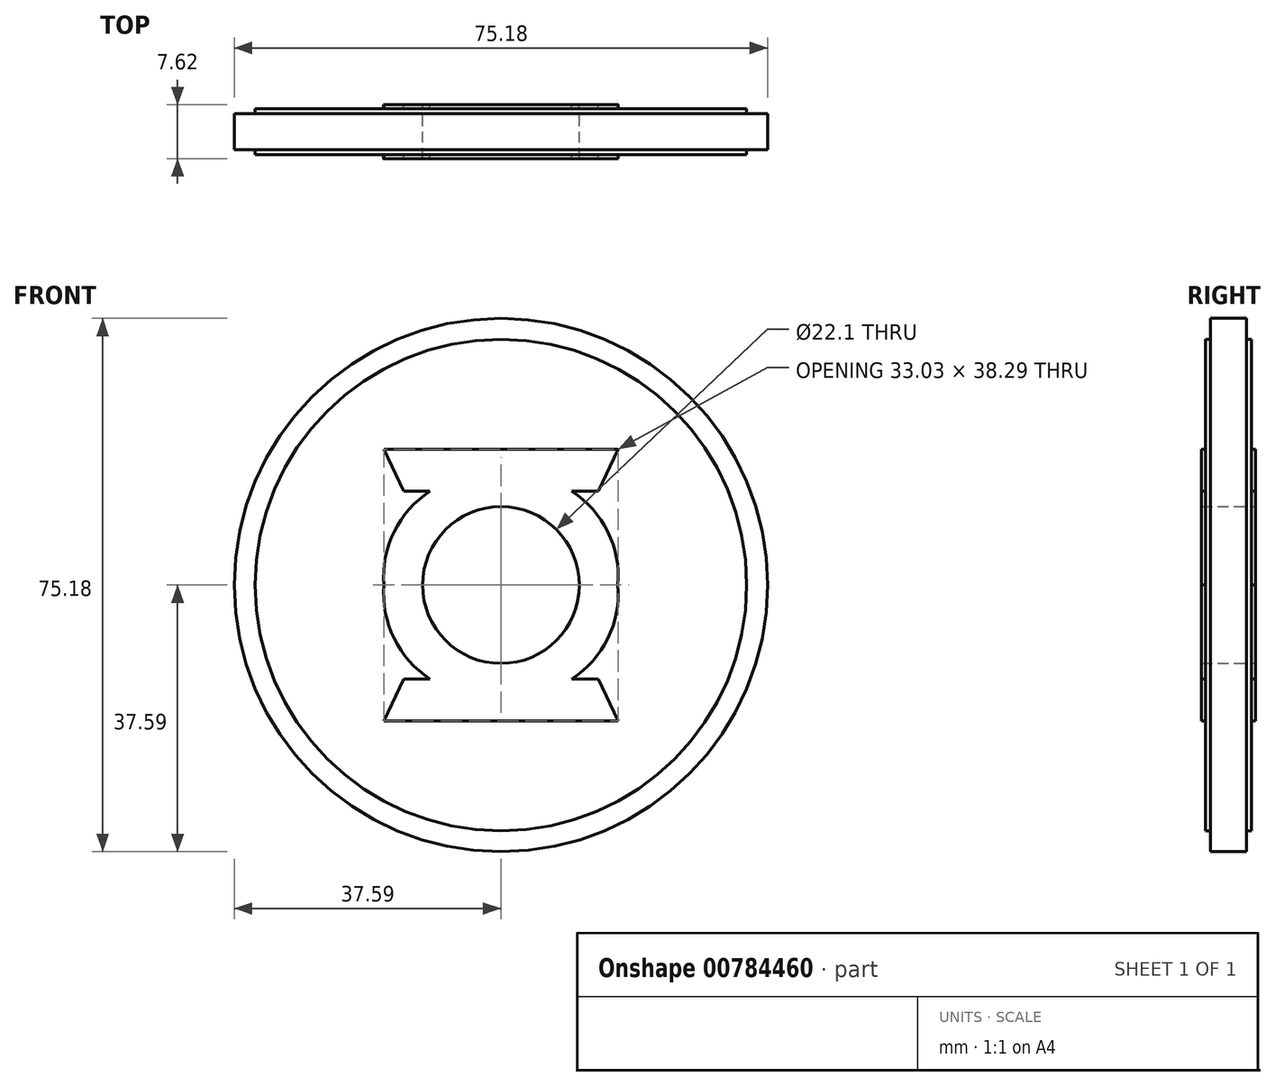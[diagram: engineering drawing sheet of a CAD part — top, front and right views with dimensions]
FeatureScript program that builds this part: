
annotation { "Feature Type Name" : "Feature", "Feature Type Description" : "" }
export const myFeature = defineFeature(function(context is Context, id is Id, definition is map)
    precondition{}
    {
        {
            var Q0;
            Q0=qCreatedBy(makeId("Front.planeOp"),FACE);
            var sketch = newSketch(context, id + "F0", { "sketchPlane" : qUnion([Q0])});
            skCircle(sketch, "E0", {"center": v(0, 0) * mm, "radius": 11.05 * mm});
            skArc(sketch, "E1", {"start": v(-10, 13.24) * mm, "mid": v(-15.07, 7.52) * mm, "end": v(-16.48, 0) * mm});
            skArc(sketch, "E2.MirrorCS", {"start": v(10, 13.24) * mm, "mid": v(15.07, 7.52) * mm, "end": v(16.48, 0) * mm});
            skArc(sketch, "E3.MirrorCS", {"start": v(-10, -13.24) * mm, "mid": v(-15.07, -7.52) * mm, "end": v(-16.48, 0) * mm});
            skArc(sketch, "E4.MirrorCS", {"start": v(10, -13.24) * mm, "mid": v(15.07, -7.52) * mm, "end": v(16.48, 0) * mm});
            skLineSegment(sketch, "E5", {"start": v(-10, -13.24) * mm, "end": v(-13.73, -13.24) * mm});
            skLineSegment(sketch, "E6", {"start": v(-13.73, -13.24) * mm, "end": v(-16.51, -19.15) * mm});
            skLineSegment(sketch, "E7", {"start": v(-16.51, -19.15) * mm, "end": v(16.51, -19.15) * mm});
            skLineSegment(sketch, "E8.MirrorCS", {"start": v(10, -13.24) * mm, "end": v(13.73, -13.24) * mm});
            skLineSegment(sketch, "E9.MirrorCS", {"start": v(13.73, -13.24) * mm, "end": v(16.51, -19.15) * mm});
            skLineSegment(sketch, "E10.MirrorCS", {"start": v(-16.51, 19.15) * mm, "end": v(16.51, 19.15) * mm});
            skLineSegment(sketch, "E11.MirrorCS", {"start": v(-13.73, 13.24) * mm, "end": v(-16.51, 19.15) * mm});
            skLineSegment(sketch, "E12.MirrorCS", {"start": v(-10, 13.24) * mm, "end": v(-13.73, 13.24) * mm});
            skLineSegment(sketch, "E13.MirrorCS", {"start": v(10, 13.24) * mm, "end": v(13.73, 13.24) * mm});
            skLineSegment(sketch, "E14.MirrorCS", {"start": v(13.73, 13.24) * mm, "end": v(16.51, 19.15) * mm});
            skCircle(sketch, "E15", {"center": v(0, 0) * mm, "radius": 34.65 * mm});
            skCircle(sketch, "E16", {"center": v(0, 0) * mm, "radius": 37.59 * mm});
            skLineSegment(sketch, "E17", {"start": v(-10, 13.24) * mm, "end": v(10, 13.24) * mm});
            skLineSegment(sketch, "E18", {"start": v(10, -13.24) * mm, "end": v(-10, -13.24) * mm});
            skSolve(sketch);
        }
        {
            var Q0;
            Q0 = qSketchRegion(id + "F0", true);
            extrude(context, id + "F1", {"entities" : qUnion([Q0]), "endBound" : BoundingType.SYMMETRIC, "depth" : 5.08 * mm, "offsetDistance" : 25.4 * mm});
        }
        {
            var Q0;
            Q0=makeQuery(id+"F0.imprint","IMPRINT",FACE,{"disambiguationData":[TD([[makeQuery(id+"F0.imprint","IMPRINT",EDGE,{"derivedFrom":sQuery(id+"F0.wireOp",EDGE,"E1")}),-1.0]])]});
            extrude(context, id + "F2", {"entities" : qUnion([Q0]), "operationType" : NewBodyOperationType.ADD, "endBound" : BoundingType.SYMMETRIC, "depth" : 6.48 * mm, "offsetDistance" : 25.4 * mm});
        }
        {
            var Q0;
            Q0=makeQuery(id+"F0.imprint","IMPRINT",FACE,{"disambiguationData":[TD([[makeQuery(id+"F0.imprint","IMPRINT",EDGE,{"derivedFrom":sQuery(id+"F0.wireOp",EDGE,"E10.MirrorCS")}),-1.0]])]});
            var Q1;
            Q1=makeQuery(id+"F0.imprint","IMPRINT",FACE,{"disambiguationData":[TD([[makeQuery(id+"F0.imprint","IMPRINT",EDGE,{"derivedFrom":sQuery(id+"F0.wireOp",EDGE,"E5")}),1.0]])]});
            extrude(context, id + "F3", {"entities" : qUnion([Q0, Q1]), "operationType" : NewBodyOperationType.ADD, "endBound" : BoundingType.SYMMETRIC, "depth" : 7.62 * mm, "offsetDistance" : 25.4 * mm});
        }
        {
            var Q0;
            Q0=makeQuery(id+"F0.imprint","IMPRINT",FACE,{"disambiguationData":[TD([[makeQuery(id+"F0.imprint","IMPRINT",EDGE,{"derivedFrom":sQuery(id+"F0.wireOp",EDGE,"E0")}),-1.0]])]});
            extrude(context, id + "F4", {"entities" : qUnion([Q0]), "operationType" : NewBodyOperationType.ADD, "endBound" : BoundingType.SYMMETRIC, "depth" : 7.62 * mm, "offsetDistance" : 25.4 * mm});
        }
    });
